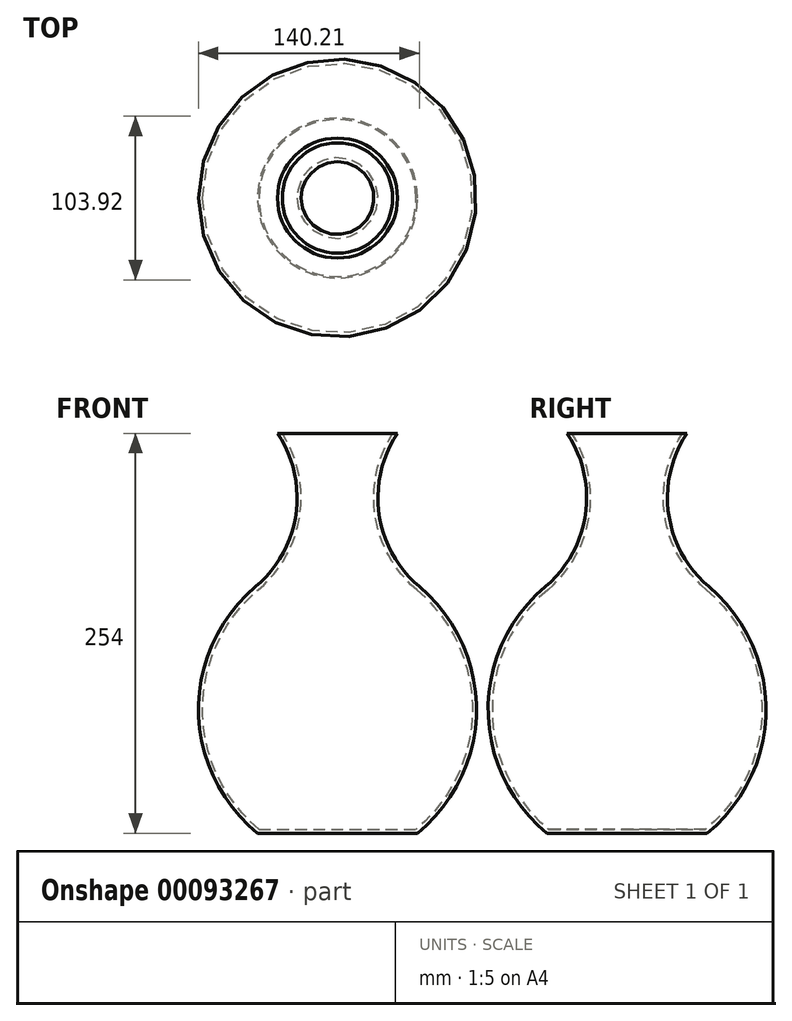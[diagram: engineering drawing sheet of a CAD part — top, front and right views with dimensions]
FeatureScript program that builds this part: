
annotation { "Feature Type Name" : "Feature", "Feature Type Description" : "" }
export const myFeature = defineFeature(function(context is Context, id is Id, definition is map)
    precondition{}
    {
        {
            var Q0;
            Q0=qCreatedBy(makeId("Front.planeOp"),FACE);
            var sketch = newSketch(context, id + "F0", { "sketchPlane" : qUnion([Q0])});
            skLineSegment(sketch, "E0", {"start": v(0, 0) * mm, "end": v(0, 254) * mm});
            skLineSegment(sketch, "E1", {"start": v(0, 254) * mm, "end": v(38.1, 254) * mm});
            skLineSegment(sketch, "E2", {"start": v(0, 0) * mm, "end": v(50.8, 0) * mm});
            skArc(sketch, "E3", {"start": v(50.8, 0) * mm, "mid": v(88.24, 78.03) * mm, "end": v(51.96, 156.6) * mm});
            skArc(sketch, "E4", {"start": v(38.1, 254) * mm, "mid": v(26.39, 202.65) * mm, "end": v(51.96, 156.6) * mm});
            skSolve(sketch);
        }
        {
            var Q0;
            Q0 = qSketchRegion(id + "F0", true);
            var Q1;
            Q1=sQuery(id+"F0.wireOp",EDGE,"E0");
            revolve(context, id + "F1", {"entities" : qUnion([Q0]), "axis" : qUnion([Q1]), "revolveType" : RevolveType.FULL});
        }
        {
            var Q0;
            Q0=makeQuery(id+"F1.opRevolve","SWEPT_FACE",FACE,{"disambiguationData":[OSD([sQuery(id+"F0.wireOp",EDGE,"E1")])]});
            shell(context, id + "F2", {"entities" : qUnion([Q0]), "thickness" : 2.54 * mm});
        }
    });
